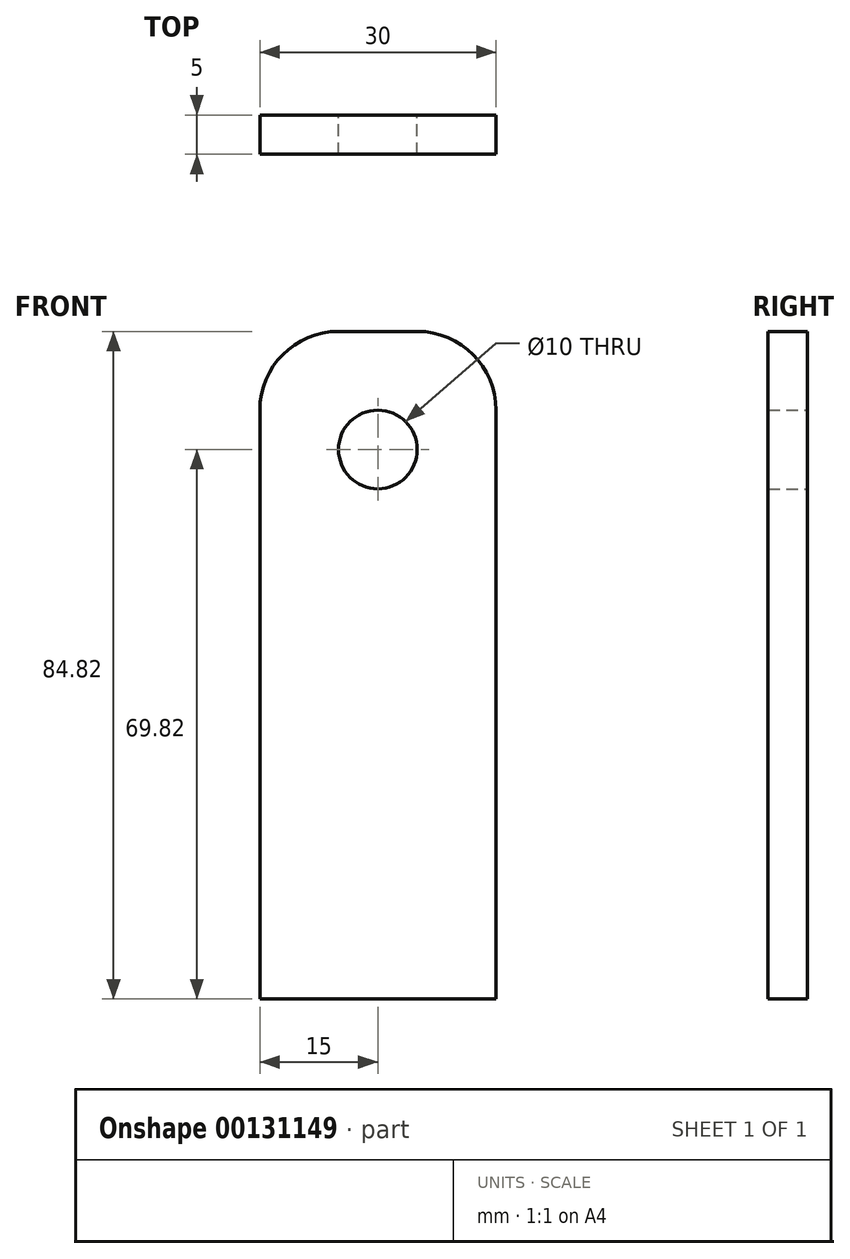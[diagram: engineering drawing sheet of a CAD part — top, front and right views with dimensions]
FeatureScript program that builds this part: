
annotation { "Feature Type Name" : "Feature", "Feature Type Description" : "" }
export const myFeature = defineFeature(function(context is Context, id is Id, definition is map)
    precondition{}
    {
        {
            var Q0;
            Q0=qCreatedBy(makeId("Front.planeOp"),FACE);
            var sketch = newSketch(context, id + "F0", { "sketchPlane" : qUnion([Q0])});
            skLineSegment(sketch, "E0.bottom", {"start": v(15, 42.4) * mm, "end": v(-15, 42.4) * mm});
            skLineSegment(sketch, "E0.top", {"start": v(15, -42.4) * mm, "end": v(-15, -42.4) * mm});
            skLineSegment(sketch, "E0.left", {"start": v(15, 42.4) * mm, "end": v(15, -42.4) * mm});
            skLineSegment(sketch, "E0.right", {"start": v(-15, 42.4) * mm, "end": v(-15, -42.4) * mm});
            skPoint(sketch, "E0.middle", {"position": v(0, 0) * mm});
            skCircle(sketch, "E1", {"center": v(0, 27.4) * mm, "radius": 5 * mm});
            skSolve(sketch);
        }
        {
            var Q0;
            Q0=makeQuery(id+"F0.imprint","IMPRINT",FACE,{"disambiguationData":[TD([[makeQuery(id+"F0.imprint","IMPRINT",EDGE,{"derivedFrom":sQuery(id+"F0.wireOp",EDGE,"E0.bottom")}),1.0]])]});
            extrude(context, id + "F1", {"entities" : qUnion([Q0]), "depth" : 5 * mm});
        }
        {
            var Q0;
            Q0=makeQuery(id+"F1.opExtrude","SWEPT_EDGE",EDGE,{"disambiguationData":[OSD([sQuery(id+"F0.wireOp",EDGE,"E0.bottom"),sQuery(id+"F0.wireOp",EDGE,"E0.left")])]});
            var Q1;
            Q1=makeQuery(id+"F1.opExtrude","SWEPT_EDGE",EDGE,{"disambiguationData":[OSD([sQuery(id+"F0.wireOp",EDGE,"E0.bottom"),sQuery(id+"F0.wireOp",EDGE,"E0.right")])]});
            fillet(context, id + "F2", {"entities" : qUnion([Q0, Q1]), "radius" : 10 * mm, "tangentPropagation" : true, "allowEdgeOverflow" : false});
        }
    });
